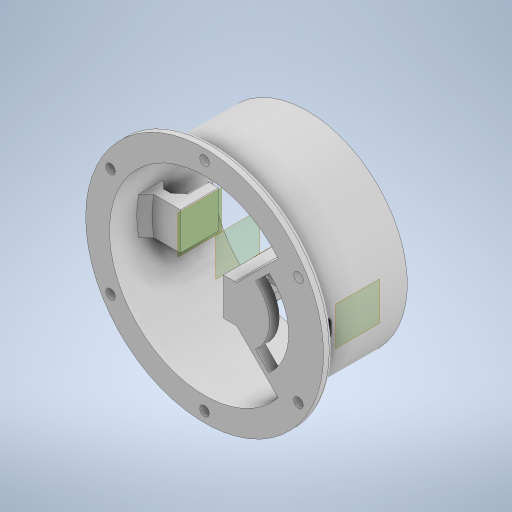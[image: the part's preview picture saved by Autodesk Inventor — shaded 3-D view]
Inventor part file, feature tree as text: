
AUTODESK INVENTOR PART (.ipt)
format: ipt  version: 2023.2 (Build 272271000, 271)  size: 1,383,936 bytes
history: native  units: mm
features: extrude x15, sketch x15, projected_geometry x10, plane x7, other x7, fillet x5, reference x3, chamfer x2
ambient origin geometry x8: Origin, YZ Plane, XZ Plane, XY Plane, X Axis, Y Axis, Z Axis, Center Point
bodies: Solid1 (feature_tree)
feature tree (64):
  plane  "Work Plane1"
  extrude  "Extrusion1"  Depth=100.0mm
  plane  "Work Plane2"
  plane  "Work Plane3"
  plane  "Work Plane4"
  extrude  "Extrusion3"  Depth=50.0mm TaperAngle=0.0deg
  plane  "Work Plane5"
  extrude  "Extrusion7"  Depth=15.0mm TaperAngle=0.0deg
  extrude  "Extrusion8"  TaperAngle=45.0deg  [1 undecoded]
  extrude  "Extrusion9"  Depth=40.0mm
  chamfer  "Chamfer5"  Distance=5.0mm
  extrude  "Extrusion10"  Depth=2.0mm
  fillet  "Fillet1"  Radius=36.860536mm
  extrude  "Extrusion11"  Depth=105.0mm
  plane  "Work Plane6"
  extrude  "Extrusion12"  Depth=2.0mm
  chamfer  "Chamfer7"  [1 undecoded]
  extrude  "Extrusion13"  Depth=2.0mm TaperAngle=360.0deg
  extrude  "Extrusion14"  Depth=2.0mm
  extrude  "Extrusion15"  Depth=10.0mm TaperAngle=0.0deg
  extrude  "Extrusion16"  Depth=2.0mm TaperAngle=45.0deg
  sketch  "Sketch21"  dims[d52=6.525mm d53=105.0mm]
  extrude  "Extrusion17"  Depth=2.0mm
  extrude  "Extrusion18"  Depth=2.0mm
  fillet  "Fillet2"  Radius=36.860536mm
  fillet  "Fillet3"  Radius=6.525mm
  fillet  "Fillet4"  Radius=4.0mm
  plane  "Work Plane7"
  extrude  "Extrusion19"  Depth=2.0mm
  fillet  "Fillet5"  Radius=19.7mm
  sketch  "Sketch3"  dims[d0=15.0mm d1=0.0mm d5=100.0mm]
  reference  "Reference1"
  reference  "Reference2"
  sketch  "Sketch5"  dims[d6=105.0mm d7=50.0mm d8=0.0mm]
  reference  "Reference3"
  projected_geometry  "Projected Loop2"
  sketch  "Sketch10"  dims[d28=9.85mm d30=15.0mm d31=0.0mm]
  projected_geometry  "Projected Loop3"
  projected_geometry  "Projected Loop4"
  sketch  "Sketch11"  dims[d32=15.0mm d33=0.0mm d34=45.0deg]
  projected_geometry  "Projected Loop5"
  sketch  "Sketch12"  dims[d35=45.0deg d36=40.0mm]
  sketch  "Sketch13"  dims[d37=60.0mm]
  projected_geometry  "Projected Loop6"
  sketch  "Sketch14"  dims[d38=4.342145mm]
  sketch  "Sketch15"  dims[d39=9.85mm]
  sketch  "Sketch16"  dims[d40=3.0mm]
  sketch  "Sketch19"  dims[d41=3.0mm d42=5.0mm d43=0.0mm]
  projected_geometry  "Projected Loop7"
  sketch  "Sketch20"  dims[d44=4.0mm d45=2.0mm d46=45.0deg d50=125.0mm d51=36.860536mm]
  projected_geometry  "Projected Loop8"
  sketch  "Sketch22"  dims[d54=5.0mm d55=0.0mm d56=2.0mm]
  projected_geometry  "Projected Loop9"
  sketch  "Sketch23"  dims[d57=5.0mm]
  projected_geometry  "Projected Loop10"
  sketch  "Sketch24"  dims[d58=57.0mm d59=0.0mm d60=0.0mm d61=60.0mm d63=360.0deg d65=5.0mm d66=10.0mm d67=0.0mm d68=4.0mm d69=2.0mm d70=45.0deg d71=105.0mm d72=100.0mm d73=36.860536mm d74=6.525mm d75=4.0mm d76=0.0mm d77=1.0mm d78=19.7mm d79=1.7mm d80=0.0mm d81=0.0mm d82=2.5mm d83=2.5mm d84=2.5mm d85=2.5mm d86=0.0mm d87=0.0mm d88=2.0mm d89=0.0mm d90=2.0mm d91=0.0mm d93=5.0mm d94=10.0mm d95=0.0mm d96=1.0mm d97=2.0mm d98=2.0mm d99=-83.0mm d100=5.0mm d101=10.0mm d102=0.0mm d103=2.0mm]
  projected_geometry  "Projected Loop11"
  other  "<userpath> windows\Documents\Inventor\Robotska_roka\Assembly4.iam"
  other  "Assembly4.iam"
  other  "Servo Motor MG996R  With Attachments:2"
  other  "servoMotorMG996R_7"
  other  "Servo Motor MG996R  With Attachments:1"
  other  "attachmentCircular_1"
  other  "servoMotorMG996R"
note: 2 required parameter values undecoded (feature->parameter linkage not recoverable at this tier; creation-order binding heuristic only, values carry confidence <= 0.55)
